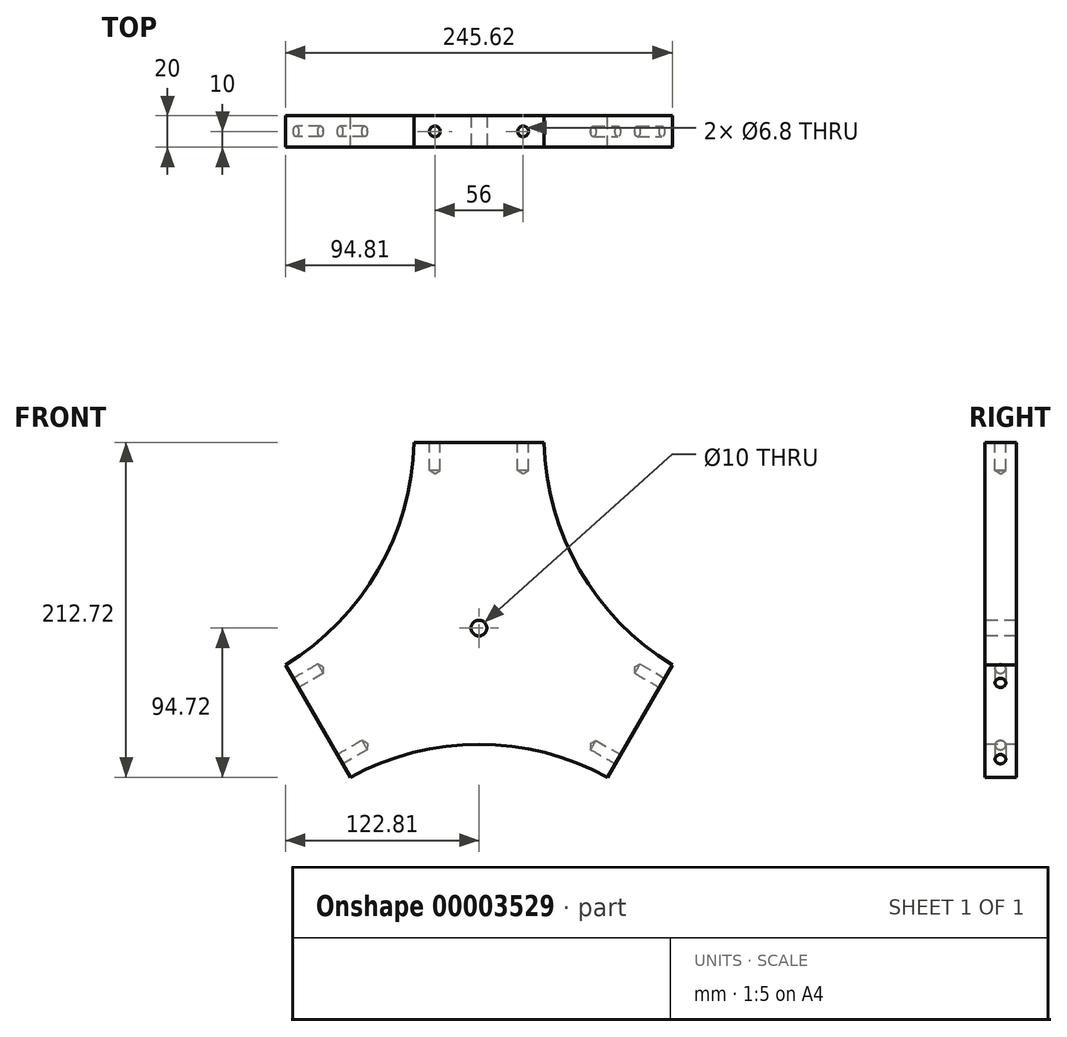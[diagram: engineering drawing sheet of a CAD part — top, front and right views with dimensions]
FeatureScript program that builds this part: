
annotation { "Feature Type Name" : "Feature", "Feature Type Description" : "" }
export const myFeature = defineFeature(function(context is Context, id is Id, definition is map)
    precondition{}
    {
        {
            var Q0;
            Q0=qCreatedBy(makeId("Front.planeOp"),FACE);
            var sketch = newSketch(context, id + "F0", { "sketchPlane" : qUnion([Q0])});
            skCircle(sketch, "E0", {"center": v(0, 0) * mm, "radius": 125 * mm});
            skLineSegment(sketch, "E1", {"start": v(0, 125) * mm, "end": v(0, 0) * mm, "construction": true});
            skLineSegment(sketch, "E2", {"start": v(-108.25, -62.5) * mm, "end": v(0, 0) * mm, "construction": true});
            skLineSegment(sketch, "E3", {"start": v(0, 0) * mm, "end": v(108.25, -62.5) * mm, "construction": true});
            skLineSegment(sketch, "E4", {"start": v(-41.24, 118) * mm, "end": v(41.24, 118) * mm});
            skLineSegment(sketch, "E5", {"start": v(-125, 0) * mm, "end": v(-97.78, -77.87) * mm});
            skLineSegment(sketch, "E6", {"start": v(97.78, -77.87) * mm, "end": v(125, 0) * mm});
            skLineSegment(sketch, "E7", {"start": v(0, 0) * mm, "end": v(-108.25, 62.5) * mm});
            skLineSegment(sketch, "E8", {"start": v(0, 0) * mm, "end": v(108.25, 62.5) * mm});
            skSolve(sketch);
        }
        {
            var Q0;
            {var subQ1=sQuery(id+"F0.wireOp",EDGE,"E4");Q0=makeQuery(id+"F0.imprint","IMPRINT",FACE,{"disambiguationData":[TD([[makeQuery(id+"F0.imprint","IMPRINT",EDGE,{"derivedFrom":subQ1}),-1.0]])]});}
            extrude(context, id + "F1", {"entities" : qUnion([Q0]), "depth" : 20 * mm});
        }
        {
            var Q0;
            Q0=makeQuery(id+"F1.opExtrude","SWEPT_FACE",FACE,{"disambiguationData":[OSD([sQuery(id+"F0.wireOp",EDGE,"E4")])]});
            var sketch = newSketch(context, id + "F2", { "sketchPlane" : qUnion([Q0])});
            skLineSegment(sketch, "E9", {"start": v(-41.24, -10) * mm, "end": v(41.24, -10) * mm, "construction": true});
            skCircle(sketch, "E10", {"center": v(-28, -10) * mm, "radius": 3.4 * mm});
            skCircle(sketch, "E11", {"center": v(28, -10) * mm, "radius": 3.4 * mm});
            skLineSegment(sketch, "E12", {"start": v(-28, -10) * mm, "end": v(0, -10) * mm, "construction": true});
            skLineSegment(sketch, "E13", {"start": v(0, -10) * mm, "end": v(28, -10) * mm, "construction": true});
            skSolve(sketch);
        }
        {
            var Q0;
            Q0 = qSketchRegion(id + "F2", true);
            extrude(context, id + "F3", {"entities" : qUnion([Q0]), "operationType" : NewBodyOperationType.REMOVE, "oppositeDirection" : true, "depth" : 20 * mm});
        }
        {
            var Q0;
            Q0=makeQuery(id+"F3.boolean.opBoolean","COPY",EDGE,{"derivedFrom":makeQuery(id+"F3.opExtrude","CAP_EDGE",EDGE,{"disambiguationData":[OSD([sQuery(id+"F2.wireOp",EDGE,"E10")])],"isStart":false})});
            var Q1;
            Q1=makeQuery(id+"F3.boolean.opBoolean","COPY",EDGE,{"derivedFrom":makeQuery(id+"F3.opExtrude","CAP_EDGE",EDGE,{"disambiguationData":[OSD([sQuery(id+"F2.wireOp",EDGE,"E11")])],"isStart":false})});
            chamfer(context, id + "F4", {"entities" : qUnion([Q0, Q1]), "chamferType" : ChamferType.OFFSET_ANGLE, "width" : (6.8 / 2) * mm, "oppositeDirection" : false, "angle" : 31 * degree, "tangentPropagation" : true});
        }
        {
            var Q0;
            Q0=makeQuery(id+"F1.opExtrude","SWEPT_BODY",BODY,{"disambiguationData":[OSD([sQuery(id+"F0.wireOp",EDGE,"E0"),sQuery(id+"F0.wireOp",EDGE,"E4"),sQuery(id+"F0.wireOp",EDGE,"E7"),sQuery(id+"F0.wireOp",EDGE,"E8")])]});
            var Q1;
            Q1=makeQuery(id+"F1.opExtrude","SWEPT_EDGE",EDGE,{"disambiguationData":[OSD([sQuery(id+"F0.wireOp",EDGE,"E7"),sQuery(id+"F0.wireOp",EDGE,"E8")])]});
            circularPattern(context, id + "F5", {"entities" : qUnion([Q0]), "axis" : qUnion([Q1]), "angle" : 120 * degree, "instanceCount" : 3});
        }
        {
            var Q0;
            Q0=makeQuery(id+"F1.opExtrude","SWEPT_BODY",BODY,{"disambiguationData":[OSD([sQuery(id+"F0.wireOp",EDGE,"E0"),sQuery(id+"F0.wireOp",EDGE,"E4"),sQuery(id+"F0.wireOp",EDGE,"E7"),sQuery(id+"F0.wireOp",EDGE,"E8")])]});
            var Q1;
            Q1=makeQuery(id+"F5.opPattern","COPY",BODY,{"derivedFrom":makeQuery(id+"F1.opExtrude","SWEPT_BODY",BODY,{"disambiguationData":[OSD([sQuery(id+"F0.wireOp",EDGE,"E0"),sQuery(id+"F0.wireOp",EDGE,"E4"),sQuery(id+"F0.wireOp",EDGE,"E7"),sQuery(id+"F0.wireOp",EDGE,"E8")])]}),"instanceName":"1"});
            var Q2;
            Q2=makeQuery(id+"F5.opPattern","COPY",BODY,{"derivedFrom":makeQuery(id+"F1.opExtrude","SWEPT_BODY",BODY,{"disambiguationData":[OSD([sQuery(id+"F0.wireOp",EDGE,"E0"),sQuery(id+"F0.wireOp",EDGE,"E4"),sQuery(id+"F0.wireOp",EDGE,"E7"),sQuery(id+"F0.wireOp",EDGE,"E8")])]}),"instanceName":"2"});
            booleanBodies(context, id + "F6", {"operationType" : BooleanOperationType.UNION, "tools" : qUnion([Q0, Q1, Q2])});
        }
        {
            var Q0;
            {var subQ0=makeQuery(id+"F1.opExtrude","CAP_FACE",FACE,{"disambiguationData":[OSD([sQuery(id+"F0.wireOp",EDGE,"E0"),sQuery(id+"F0.wireOp",EDGE,"E4"),sQuery(id+"F0.wireOp",EDGE,"E7"),sQuery(id+"F0.wireOp",EDGE,"E8")])],"isStart":false});Q0=makeQuery(id+"F6.opBoolean","MERGE",FACE,{"derivedFrom":[subQ0,makeQuery(id+"F5.opPattern","COPY",FACE,{"derivedFrom":subQ0,"instanceName":"1"}),makeQuery(id+"F5.opPattern","COPY",FACE,{"derivedFrom":subQ0,"instanceName":"2"})]});}
            var sketch = newSketch(context, id + "F7", { "sketchPlane" : qUnion([Q0])});
            skArc(sketch, "E14", {"start": v(-122.81, -23.28) * mm, "mid": v(-63.97, 36.94) * mm, "end": v(-41.24, 118) * mm});
            skArc(sketch, "E15", {"start": v(41.24, 118) * mm, "mid": v(63.97, 36.94) * mm, "end": v(122.81, -23.28) * mm});
            skArc(sketch, "E16", {"start": v(81.57, -94.72) * mm, "mid": v(0, -73.87) * mm, "end": v(-81.57, -94.72) * mm});
            skArc(sketch, "E17.0", {"start": v(-41.24, 118) * mm, "mid": v(-108.25, 62.5) * mm, "end": v(-122.81, -23.28) * mm});
            skArc(sketch, "E18.0", {"start": v(122.81, -23.28) * mm, "mid": v(108.25, 62.5) * mm, "end": v(41.24, 118) * mm});
            skArc(sketch, "E19.0", {"start": v(-81.57, -94.72) * mm, "mid": v(0, -125) * mm, "end": v(81.57, -94.72) * mm});
            skCircle(sketch, "E20", {"center": v(0, 0) * mm, "radius": 5 * mm});
            skSolve(sketch);
        }
        {
            var Q0;
            Q0=makeQuery(id+"F7.imprint","IMPRINT",FACE,{"disambiguationData":[TD([[makeQuery(id+"F7.imprint","IMPRINT",EDGE,{"derivedFrom":sQuery(id+"F7.wireOp",EDGE,"E14")}),1.0]])]});
            var Q1;
            Q1=makeQuery(id+"F7.imprint","IMPRINT",FACE,{"disambiguationData":[TD([[makeQuery(id+"F7.imprint","IMPRINT",EDGE,{"derivedFrom":sQuery(id+"F7.wireOp",EDGE,"E15")}),1.0]])]});
            var Q2;
            Q2=makeQuery(id+"F7.imprint","IMPRINT",FACE,{"disambiguationData":[TD([[makeQuery(id+"F7.imprint","IMPRINT",EDGE,{"derivedFrom":sQuery(id+"F7.wireOp",EDGE,"E16")}),1.0]])]});
            var Q3;
            Q3=makeQuery(id+"F7.imprint","IMPRINT",FACE,{"disambiguationData":[TD([[makeQuery(id+"F7.imprint","IMPRINT",EDGE,{"derivedFrom":sQuery(id+"F7.wireOp",EDGE,"E20")}),1.0]])]});
            var Q4;
            {var subQ0=makeQuery(id+"F1.opExtrude","CAP_FACE",FACE,{"disambiguationData":[OSD([sQuery(id+"F0.wireOp",EDGE,"E0"),sQuery(id+"F0.wireOp",EDGE,"E4"),sQuery(id+"F0.wireOp",EDGE,"E7"),sQuery(id+"F0.wireOp",EDGE,"E8")])],"isStart":true});Q4=makeQuery(id+"F6.opBoolean","MERGE",FACE,{"derivedFrom":[subQ0,makeQuery(id+"F5.opPattern","COPY",FACE,{"derivedFrom":subQ0,"instanceName":"1"}),makeQuery(id+"F5.opPattern","COPY",FACE,{"derivedFrom":subQ0,"instanceName":"2"})]});}
            extrude(context, id + "F8", {"entities" : qUnion([Q0, Q1, Q2, Q3]), "operationType" : NewBodyOperationType.REMOVE, "endBound" : BoundingType.UP_TO_SURFACE, "oppositeDirection" : true, "endBoundEntityFace" : qUnion([Q4]), "depth" : 25 * mm});
        }
    });
